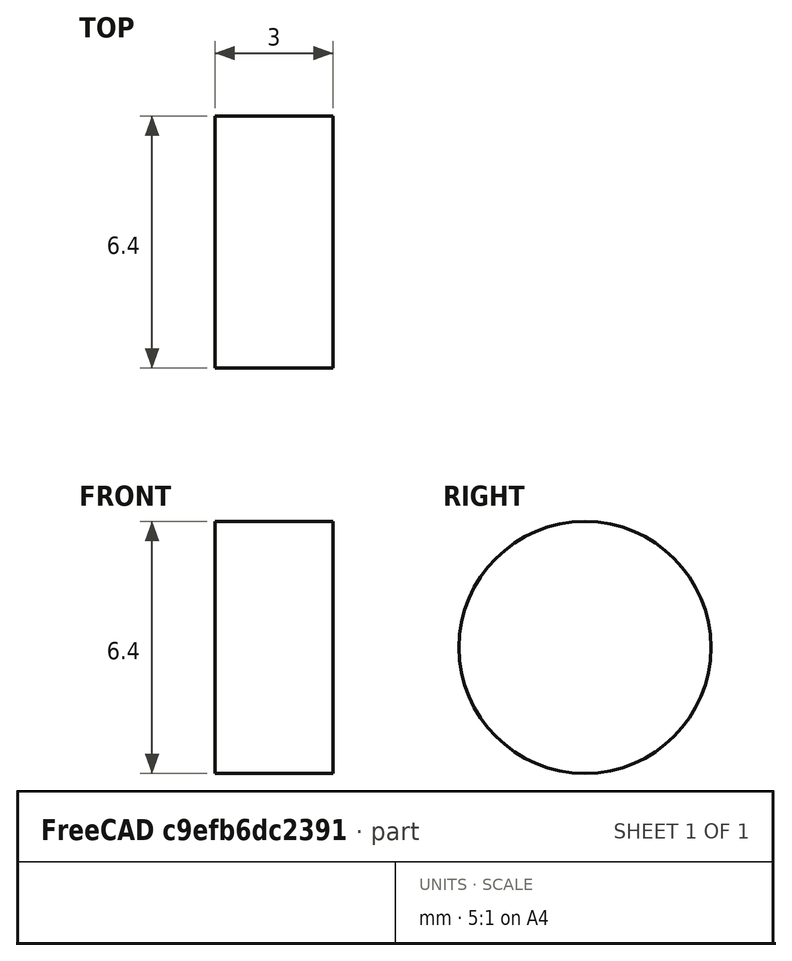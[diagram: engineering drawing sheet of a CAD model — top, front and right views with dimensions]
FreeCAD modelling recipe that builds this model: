
FCSTD DOCUMENT  (FreeCAD 0.19R)
Label: E8_D6_4_V_ShrtStub
License: All rights reserved
LicenseURL: http://en.wikipedia.org/wiki/All_rights_reserved
objects: Sketcher::SketchObject×1, PartDesign::Revolution×1, PartDesign::Body×1
note: 4 computed .brp shape members not serialized (recipe doc carries the construction recipe); baked Part::Feature solids carry a one-line shape summary decoded from their .brp

FEATURE [Sketcher::SketchObject] Sketch
  FullyConstrained = false
  MapMode = 5
  Support = -> [XY_Plane]
  sketch-geometry (7):
    g0: GeomPoint X=0 Y=3.2 Z=0
    g1: GeomPoint X=30 Y=3.2 Z=0
    g2: GeomPoint X=92.5486 Y=36.3931 Z=0
    g3: LineSegment StartX=0 StartY=0 StartZ=0 EndX=0 EndY=3.2 EndZ=0
    g4: LineSegment StartX=0 StartY=3.2 StartZ=0 EndX=3 EndY=3.2 EndZ=0
    g5: LineSegment StartX=3 StartY=3.2 StartZ=0 EndX=3 EndY=-4e-16 EndZ=0
    g6: LineSegment StartX=0 StartY=0 StartZ=0 EndX=3 EndY=-6e-16 EndZ=0
  constraints (12):
    c: Coincident(g3,g-1)
    c: Coincident(g3,g0)
    c: Vertical(g3)
    c: Coincident(g4,g3)
    c: Horizontal(g4)
    c: DistanceX(g4,g4) = 3
    c: Coincident(g5,g4)
    c: Vertical(g5)
    c: Coincident(g6,g3)
    c: Coincident(g6,g5)
    c: DistanceY(g3,g3) = 3.2
    c: Parallel(g4,g6)
FEATURE [PartDesign::Revolution] Revolution
  Angle = 360
  Axis = (1,0,0)
  Base = (0,0,0)
  Profile = -> Sketch
  ReferenceAxis = -> Sketch [H_Axis]
FEATURE [PartDesign::Body] Body
  Group = -> [Sketch,Revolution]
  Origin = -> Origin
  Tip = -> Revolution
